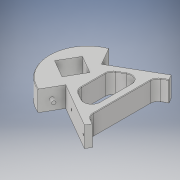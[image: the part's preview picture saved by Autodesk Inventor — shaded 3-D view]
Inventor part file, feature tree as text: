
AUTODESK INVENTOR PART (.ipt)
format: ipt  version: 2019 (Build 230136000, 136)  size: 245,248 bytes
history: native  units: mm
features: sketch x6, fillet x5, extrude x4, hole x2
ambient origin geometry x8: Origin, YZ Plane, XZ Plane, XY Plane, X Axis, Y Axis, Z Axis, Center Point
bodies: Solid1 (feature_tree)
feature tree (17):
  extrude  "Extrusion1"  Depth=100.0mm
  extrude  "Extrusion2"  Depth=20.0mm
  extrude  "Extrusion3"  Depth=6.8mm
  extrude  "Extrusion4"  Depth=10.0mm
  fillet  "Fillet1"  Radius=10.0mm
  fillet  "Fillet2"  Radius=40.0mm
  fillet  "Fillet3"  Radius=40.0mm
  hole  "Hole1"  [1 undecoded]
  hole  "Hole2"  [1 undecoded]
  fillet  "Fillet8"  Radius=40.0mm
  fillet  "Fillet9"  Radius=15.0mm
  sketch  "Sketch1"  dims[d3=40.0mm d4=100.0mm]
  sketch  "Sketch2"  dims[d5=12.0mm d7=20.0mm]
  sketch  "Sketch3"  dims[d8=40.0mm d9=0.0mm d10=6.8mm]
  sketch  "Sketch4"  dims[d11=10.0mm d12=0.0mm d13=6.8mm d14=10.0mm d15=0.0mm d16=40.0mm d17=40.0mm]
  sketch  "Sketch5"  dims[d19=70.0mm d20=75.0mm]
  sketch  "Sketch6"  dims[d21=15.0mm d22=50.0mm d24=40.0mm d25=0.0mm d26=15.0mm d27=15.0mm d28=15.0mm d29=4.0mm d30=6.0mm d31=5.0mm d32=2.0mm d33=14.3117mm d34=4.0mm d35=0.0mm d36=4.0mm d37=6.0mm d38=5.0mm d39=2.0mm d40=14.3117mm d41=4.0mm d42=0.0mm d47=1.0mm d48=1.0mm d49=20.0mm]
note: 2 required parameter values undecoded (feature->parameter linkage not recoverable at this tier; creation-order binding heuristic only, values carry confidence <= 0.55)
